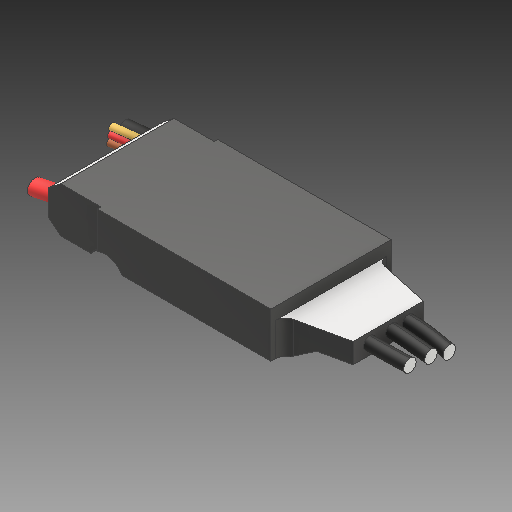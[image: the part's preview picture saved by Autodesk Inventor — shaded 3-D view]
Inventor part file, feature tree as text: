
AUTODESK INVENTOR PART (.ipt)
format: ipt  version: 2018 (Build 220112000, 112)  size: 986,112 bytes
history: native  units: mm
features: other x3, sketch x1
ambient origin geometry x8: Origin, YZ Plane, XZ Plane, XY Plane, X Axis, Y Axis, Z Axis, Center Point
bodies: Volumenkörper1 (feature_tree)
feature tree (4):
  other  "28-2-2013-001 - ESC Flyduino SimonK 20A body.ipt"
  other  "Volumenkörper1::28-2-2013-001 - ESC Flyduino SimonK 20A body.ipt"
  other  "Bezeichnung1"
  sketch  "Skizze1"  dims[d0=10.0mm]
